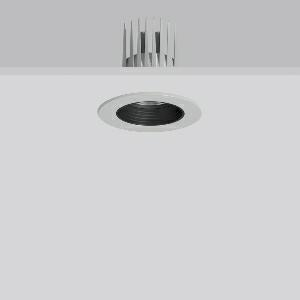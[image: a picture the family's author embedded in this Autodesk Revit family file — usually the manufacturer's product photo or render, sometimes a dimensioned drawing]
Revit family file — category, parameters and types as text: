
# Revit family: heledon_mini_e_901754_004_1_76_aaf8
name_source: partatom
category: Lighting Fixtures
units: mm (PartAtom-declared; Revit-internal decimal feet)

## family parameters
Cut with Voids When Loaded = No
Host = Face
Light Source = No
Part Type = Normal
Room Calculation Point = No
Round Connector Dimension = Use Diameter
Shared = No

## types (1)
- HELEDON mini E (1 x LED Modul 940, 3500 lm, 4000)
    Apparent Load = 29 VA
    Approval mark = CE
    CIE Flux Codes = 80 99 100 100 100
    Color Rendering = 92
    Color Temperature = 4000
    Default Elevation = 1800 mm
    Description = Series: HELEDON mini
Round recessed downlight. Housing: die-cast aluminium, powder-coated. Black plastic ring and recessed LED to prevent glare from the side. Optical assembly with lens made of plastic (polycarbonate) for the best homogeneous light distribution - can be changed without tools. Best colour rendering index Ra>90. Suitable for Recessed ceiling mounting. Installation without tools thanks to spring fastening system. Including separate LED converter with connecting cable 600 mm.High quality converter without flickering and stroboscopic effect. Through-wiring box (5 pole) available as accessory. The following accessories can be mounted without use of tools: interchangeable lenses, decorative glasses, honeycomb louvre, clear and frosted diffusers, white interchangeable plastic ring. 
Colour: silver
Diameter: 124 mm
Height: 3 mm
Cut-out diameter: 114 mm
Recess height: 170 mm
Luminaire: recess height: 120 mm
Lamp: LED
Socket: without socket
Colour temperature: 4000K
Colour rendering index (CRI): 92
System power: 29 W
Rated luminous flux: 3500 lm
Luminous efficiency: 121 lm/W
Control gear: Converter, dimmable, DALI
Protection class: II
Type of protection: IP 20
    Height = 0 mm  [stored 0 ft]
    Lamp = 1 x LED Modul 940
    Lamp Light Flux = 3500 lm
    Lamp count = 1
    Length = 124 mm  [stored 0.406824 ft]
    Lifetime = 50000 h
    Luminous efficacy = 121 lm/W
    Manufacturer = RZB
    ModVariant = No
    Model = 901754.004.1.76
    Mounting Place = Ceiling
    Mounting Type = Recessed
    Number of Poles = 1
    OnlyDefault = Yes
    Power Factor = 1
    Product Name = HELEDON mini E
    Product group = Recessed downlights
    ProductGroupID = 402
    Protection Class = Protection class II
    Protection Degree = IP 20
    RLX_Detail_Level = 1
    RLX_Emergency_Light_Flux = 0 lm
    RLX_Emergency_Type = 0
    RLX_Emergency_Type_DB = No
    RlxData = <blob elided: 127813 chars, md5=e1f1d971>
    Socket = socket
    Standby Power = 0 W
    System Light Flux = 3500 lm
    System Power = 29 W
    Type Comments = Product without accessories
    Type Image = 901656.004.jpg
    URL = http://relux.com
    VarID = ---
    Voltage = 230 V
    Voltage Range = 220-240 V
    Weight = 0.00 kg
    Width = 0 mm  [stored 0 ft]

note: [stored X ft] marks values corroborated as IEEE doubles in the binary element streams (Revit-internal decimal feet)

## geometry (parser evidence)
native form markers: Blend x4, Sweep x11
no freeform markers — native parametric forms only
